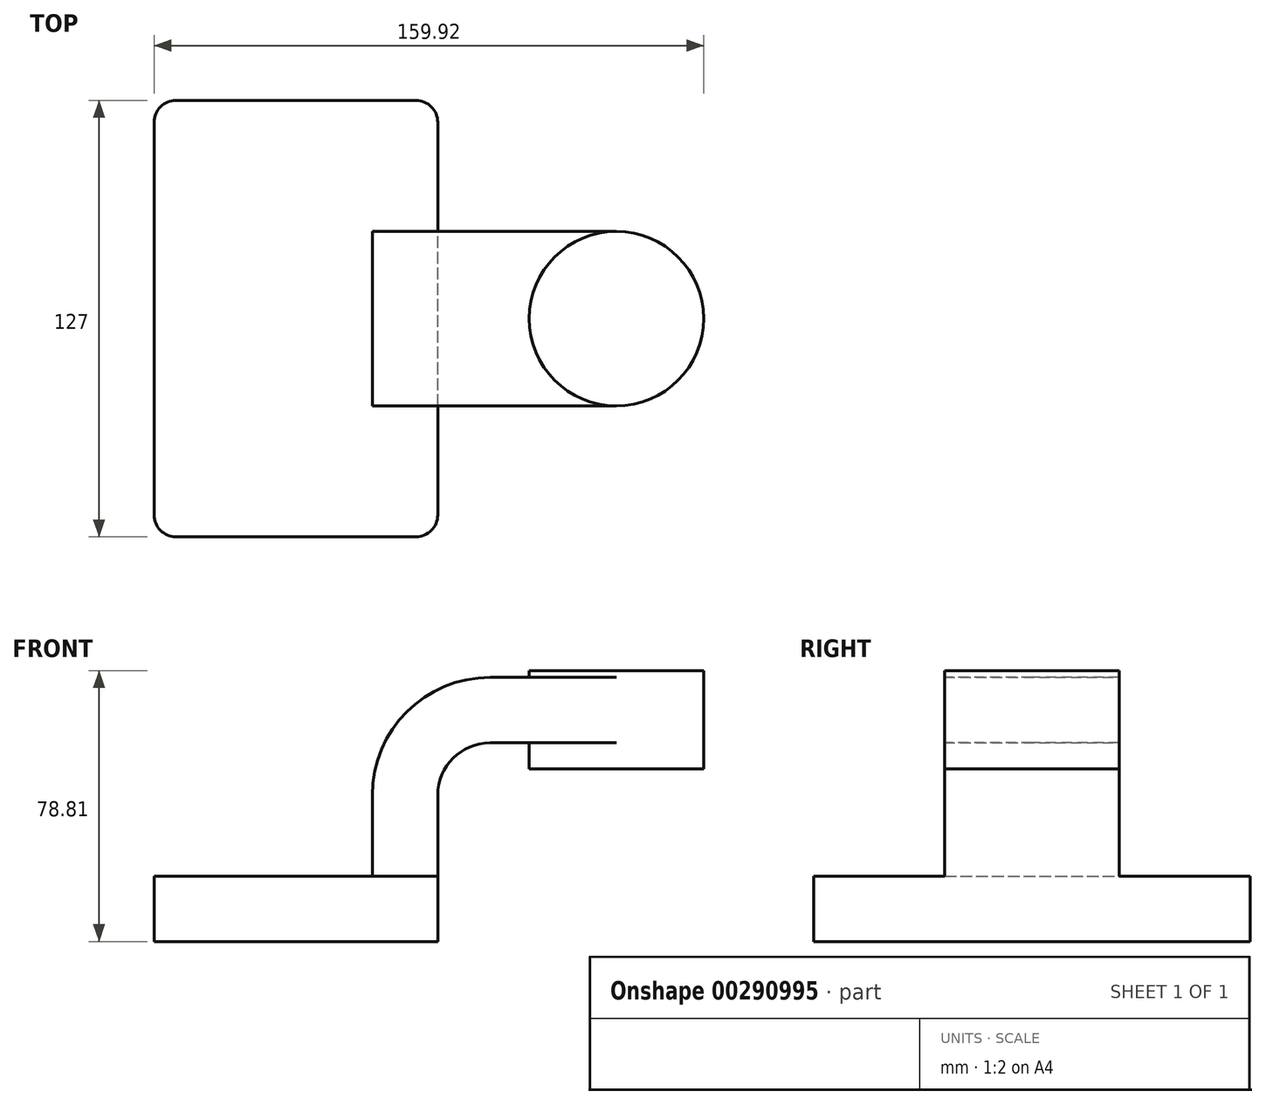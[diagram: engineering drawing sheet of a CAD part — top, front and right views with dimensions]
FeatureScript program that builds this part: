
annotation { "Feature Type Name" : "Feature", "Feature Type Description" : "" }
export const myFeature = defineFeature(function(context is Context, id is Id, definition is map)
    precondition{}
    {
        {
            var Q0;
            Q0=qCreatedBy(makeId("Front.planeOp"),FACE);
            var sketch = newSketch(context, id + "F0", { "sketchPlane" : qUnion([Q0])});
            skLineSegment(sketch, "E0.bottom", {"start": v(-41.28, -9.53) * mm, "end": v(41.28, -9.53) * mm});
            skLineSegment(sketch, "E0.top", {"start": v(-41.28, 9.53) * mm, "end": v(41.28, 9.53) * mm});
            skLineSegment(sketch, "E0.left", {"start": v(-41.28, -9.53) * mm, "end": v(-41.28, 9.53) * mm});
            skLineSegment(sketch, "E0.right", {"start": v(41.28, -9.53) * mm, "end": v(41.28, 9.53) * mm});
            skPoint(sketch, "E0.middle", {"position": v(0, 0) * mm});
            skLineSegment(sketch, "E1.bottom", {"start": v(67.85, 40.7) * mm, "end": v(118.65, 40.7) * mm});
            skLineSegment(sketch, "E1.top", {"start": v(67.85, 69.28) * mm, "end": v(118.65, 69.28) * mm});
            skLineSegment(sketch, "E1.left", {"start": v(67.85, 40.7) * mm, "end": v(67.85, 69.28) * mm});
            skLineSegment(sketch, "E1.right", {"start": v(118.65, 40.7) * mm, "end": v(118.65, 69.28) * mm});
            skPoint(sketch, "E1.middle", {"position": v(93.25, 55) * mm});
            skLineSegment(sketch, "E2", {"start": v(41.27, 9.53) * mm, "end": v(41.27, 33.07) * mm});
            skArc(sketch, "E3", {"start": v(41.27, 33.07) * mm, "mid": v(45.74, 43.85) * mm, "end": v(56.51, 48.3) * mm});
            skLineSegment(sketch, "E4", {"start": v(56.51, 48.3) * mm, "end": v(139.06, 48.3) * mm});
            skLineSegment(sketch, "E5.0", {"start": v(56.51, 67.36) * mm, "end": v(139.06, 67.36) * mm});
            skArc(sketch, "E5.1", {"start": v(22.22, 33.07) * mm, "mid": v(32.27, 57.32) * mm, "end": v(56.51, 67.36) * mm});
            skLineSegment(sketch, "E5.2", {"start": v(22.23, 9.53) * mm, "end": v(22.23, 33.07) * mm});
            skLineSegment(sketch, "E6", {"start": v(93.25, 40.7) * mm, "end": v(93.25, 69.28) * mm});
            skLineSegment(sketch, "E7", {"start": v(139.06, 67.36) * mm, "end": v(139.06, 48.3) * mm});
            skFitSpline(sketch, "E8", {"points": [v(-41.28, 9.52) * mm, v(56.51, 67.36) * mm], "startDerivative": vector(54.97, 148.73) * mm, "endDerivative": vector(126.51, -4.49) * mm});
            skSolve(sketch);
        }
        {
            var Q0;
            Q0=makeQuery(id+"F0.imprint","IMPRINT",FACE,{"disambiguationData":[TD([[makeQuery(id+"F0.imprint","IMPRINT",EDGE,{"derivedFrom":sQuery(id+"F0.wireOp",EDGE,"E0.bottom")}),1.0]])]});
            extrude(context, id + "F1", {"entities" : qUnion([Q0]), "endBound" : BoundingType.SYMMETRIC, "depth" : 127 * mm});
        }
        {
            var Q0;
            {var subQ1=sQuery(id+"F0.wireOp",EDGE,"E2");Q0=makeQuery(id+"F0.imprint","IMPRINT",FACE,{"disambiguationData":[TD([[makeQuery(id+"F0.imprint","IMPRINT",EDGE,{"derivedFrom":subQ1}),1.0]])]});}
            var Q1;
            {var subQ0=sQuery(id+"F0.wireOp",EDGE,"E4");var subQ1=sQuery(id+"F0.wireOp",EDGE,"E1.left");var subQ2=makeQuery(id+"F0.imprint","INTERSECT",VERTEX,{"derivedFrom":[subQ1,subQ0]});Q1=makeQuery(id+"F0.imprint","IMPRINT",FACE,{"disambiguationData":[TD([[makeQuery(id+"F0.imprint","IMPRINT",EDGE,{"disambiguationData":[TD([[subQ2,-1.0]])],"derivedFrom":subQ1}),-1.0]])]});}
            extrude(context, id + "F2", {"entities" : qUnion([Q0, Q1]), "operationType" : NewBodyOperationType.ADD, "endBound" : BoundingType.SYMMETRIC, "depth" : 50.8 * mm});
        }
        {
            var Q0;
            Q0=makeQuery(id+"F0.imprint","IMPRINT",FACE,{"disambiguationData":[TD([[makeQuery(id+"F0.imprint","IMPRINT",EDGE,{"derivedFrom":sQuery(id+"F0.wireOp",EDGE,"E5.1")}),1.0]])]});
            extrude(context, id + "F3", {"entities" : qUnion([Q0]), "operationType" : NewBodyOperationType.ADD, "endBound" : BoundingType.SYMMETRIC, "depth" : 15.88 * mm});
        }
        {
            var Q0;
            {var subQ0=sQuery(id+"F0.wireOp",EDGE,"E1.right");var subQ1=sQuery(id+"F0.wireOp",EDGE,"E1.bottom");var subQ2=makeQuery(id+"F0.imprint","INTERSECT",VERTEX,{"derivedFrom":[subQ1,subQ0]});Q0=makeQuery(id+"F0.imprint","IMPRINT",FACE,{"disambiguationData":[TD([[makeQuery(id+"F0.imprint","IMPRINT",EDGE,{"disambiguationData":[TD([[subQ2,1.0]])],"derivedFrom":subQ1}),1.0]])]});}
            var Q1;
            {var subQ0=sQuery(id+"F0.wireOp",EDGE,"E4");var subQ1=sQuery(id+"F0.wireOp",EDGE,"E1.right");var subQ2=makeQuery(id+"F0.imprint","INTERSECT",VERTEX,{"derivedFrom":[subQ1,subQ0]});Q1=makeQuery(id+"F0.imprint","IMPRINT",FACE,{"disambiguationData":[TD([[makeQuery(id+"F0.imprint","IMPRINT",EDGE,{"disambiguationData":[TD([[subQ2,-1.0]])],"derivedFrom":subQ1}),1.0]])]});}
            var Q2;
            {var subQ0=sQuery(id+"F0.wireOp",EDGE,"E1.right");var subQ1=sQuery(id+"F0.wireOp",EDGE,"E1.top");var subQ2=makeQuery(id+"F0.imprint","INTERSECT",VERTEX,{"derivedFrom":[subQ1,subQ0]});Q2=makeQuery(id+"F0.imprint","IMPRINT",FACE,{"disambiguationData":[TD([[makeQuery(id+"F0.imprint","IMPRINT",EDGE,{"disambiguationData":[TD([[subQ2,1.0]])],"derivedFrom":subQ1}),-1.0]])]});}
            var Q3;
            Q3=sQuery(id+"F0.wireOp",EDGE,"E6");
            revolve(context, id + "F4", {"operationType" : NewBodyOperationType.ADD, "entities" : qUnion([Q0, Q1, Q2]), "axis" : qUnion([Q3]), "revolveType" : RevolveType.FULL});
        }
        {
            var Q0;
            Q0=makeQuery(id+"F1.opExtrude","CAP_EDGE",EDGE,{"disambiguationData":[OSD([sQuery(id+"F0.wireOp",EDGE,"E0.left")])],"isStart":false});
            var Q1;
            Q1=makeQuery(id+"F1.opExtrude","CAP_EDGE",EDGE,{"disambiguationData":[OSD([sQuery(id+"F0.wireOp",EDGE,"E0.right")])],"isStart":false});
            var Q2;
            Q2=makeQuery(id+"F1.opExtrude","CAP_EDGE",EDGE,{"disambiguationData":[OSD([sQuery(id+"F0.wireOp",EDGE,"E0.right")])],"isStart":true});
            var Q3;
            Q3=makeQuery(id+"F1.opExtrude","CAP_EDGE",EDGE,{"disambiguationData":[OSD([sQuery(id+"F0.wireOp",EDGE,"E0.left")])],"isStart":true});
            fillet(context, id + "F5", {"entities" : qUnion([Q0, Q1, Q2, Q3]), "radius" : 6.35 * mm, "tangentPropagation" : true, "allowEdgeOverflow" : false});
        }
    });
